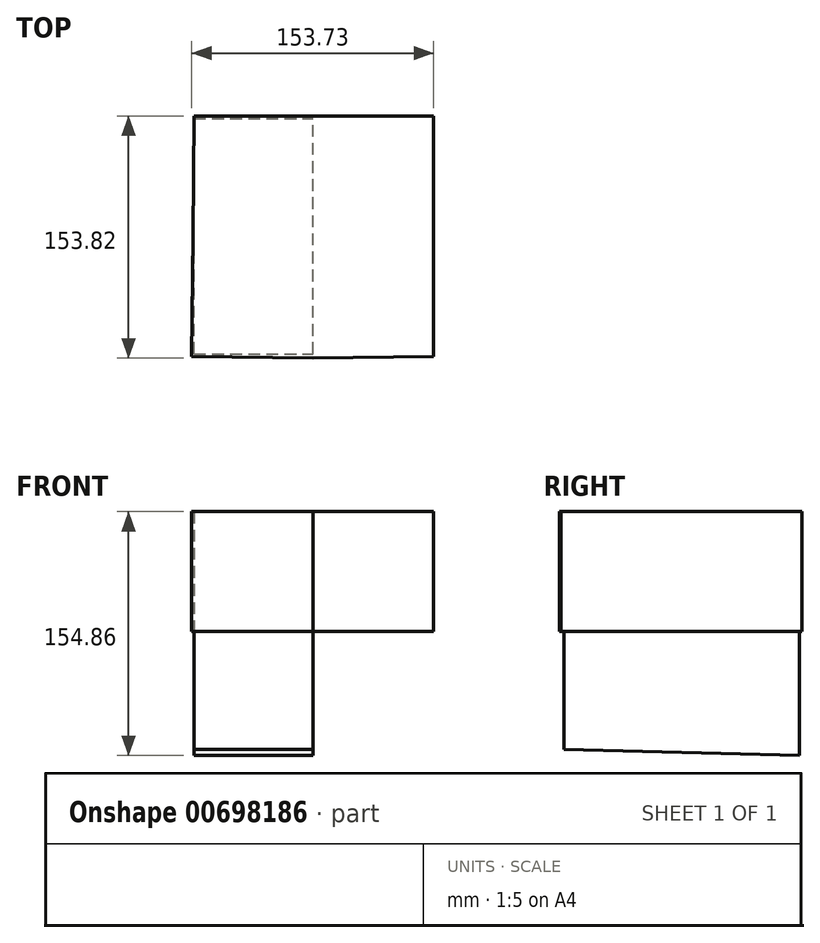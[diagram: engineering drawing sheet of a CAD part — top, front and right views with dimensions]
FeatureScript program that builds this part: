
annotation { "Feature Type Name" : "Feature", "Feature Type Description" : "" }
export const myFeature = defineFeature(function(context is Context, id is Id, definition is map)
    precondition{}
    {
        {
            var Q0;
            Q0=qCreatedBy(makeId("Top.planeOp"),FACE);
            var sketch = newSketch(context, id + "F0", { "sketchPlane" : qUnion([Q0])});
            skLineSegment(sketch, "E0", {"start": v(0, 0) * mm, "end": v(-75.67, 76.05) * mm});
            skLineSegment(sketch, "E1", {"start": v(0, 0) * mm, "end": v(76.43, 76.05) * mm});
            skLineSegment(sketch, "E2", {"start": v(0, 0) * mm, "end": v(76.43, -76.8) * mm});
            skLineSegment(sketch, "E3", {"start": v(0, 0) * mm, "end": v(-77.19, -76.8) * mm});
            skLineSegment(sketch, "E4", {"start": v(0, 0) * mm, "end": v(76.54, 0) * mm});
            skLineSegment(sketch, "E5", {"start": v(0, 0) * mm, "end": v(-76.28, 0) * mm});
            skLineSegment(sketch, "E6", {"start": v(0, 0) * mm, "end": v(0, -77.75) * mm});
            skLineSegment(sketch, "E7", {"start": v(0, 0) * mm, "end": v(0, 76.07) * mm});
            skLineSegment(sketch, "E8", {"start": v(76.43, 76.05) * mm, "end": v(0, 76.07) * mm});
            skLineSegment(sketch, "E9", {"start": v(0, 76.07) * mm, "end": v(-75.67, 76.05) * mm});
            skLineSegment(sketch, "E10", {"start": v(-75.67, 76.05) * mm, "end": v(-76.28, 0) * mm});
            skLineSegment(sketch, "E11", {"start": v(-76.28, 0) * mm, "end": v(-77.19, -76.8) * mm});
            skLineSegment(sketch, "E12", {"start": v(-77.19, -76.8) * mm, "end": v(0, -77.75) * mm});
            skLineSegment(sketch, "E13", {"start": v(0, -77.75) * mm, "end": v(76.43, -76.8) * mm});
            skLineSegment(sketch, "E14", {"start": v(76.43, -76.8) * mm, "end": v(76.54, 0) * mm});
            skLineSegment(sketch, "E15", {"start": v(76.54, 0) * mm, "end": v(76.43, 76.05) * mm});
            skSolve(sketch);
        }
        {
            var Q0;
            Q0=makeQuery(id+"F0.imprint","IMPRINT",FACE,{"disambiguationData":[TD([[makeQuery(id+"F0.imprint","IMPRINT",EDGE,{"derivedFrom":sQuery(id+"F0.wireOp",EDGE,"E0")}),1.0]])]});
            var Q1;
            Q1=makeQuery(id+"F0.imprint","IMPRINT",FACE,{"disambiguationData":[TD([[makeQuery(id+"F0.imprint","IMPRINT",EDGE,{"derivedFrom":sQuery(id+"F0.wireOp",EDGE,"E0")}),-1.0]])]});
            var Q2;
            Q2=makeQuery(id+"F0.imprint","IMPRINT",FACE,{"disambiguationData":[TD([[makeQuery(id+"F0.imprint","IMPRINT",EDGE,{"derivedFrom":sQuery(id+"F0.wireOp",EDGE,"E2")}),1.0]])]});
            var Q3;
            Q3=makeQuery(id+"F0.imprint","IMPRINT",FACE,{"disambiguationData":[TD([[makeQuery(id+"F0.imprint","IMPRINT",EDGE,{"derivedFrom":sQuery(id+"F0.wireOp",EDGE,"E2")}),-1.0]])]});
            var Q4;
            Q4=makeQuery(id+"F0.imprint","IMPRINT",FACE,{"disambiguationData":[TD([[makeQuery(id+"F0.imprint","IMPRINT",EDGE,{"derivedFrom":sQuery(id+"F0.wireOp",EDGE,"E3")}),-1.0]])]});
            var Q5;
            Q5=makeQuery(id+"F0.imprint","IMPRINT",FACE,{"disambiguationData":[TD([[makeQuery(id+"F0.imprint","IMPRINT",EDGE,{"derivedFrom":sQuery(id+"F0.wireOp",EDGE,"E3")}),1.0]])]});
            var Q6;
            Q6=makeQuery(id+"F0.imprint","IMPRINT",FACE,{"disambiguationData":[TD([[makeQuery(id+"F0.imprint","IMPRINT",EDGE,{"derivedFrom":sQuery(id+"F0.wireOp",EDGE,"E1")}),-1.0]])]});
            var Q7;
            Q7=makeQuery(id+"F0.imprint","IMPRINT",FACE,{"disambiguationData":[TD([[makeQuery(id+"F0.imprint","IMPRINT",EDGE,{"derivedFrom":sQuery(id+"F0.wireOp",EDGE,"E1")}),1.0]])]});
            extrude(context, id + "F1", {"entities" : qUnion([Q0, Q1, Q2, Q3, Q4, Q5, Q6, Q7]), "depth" : 76.2 * mm, "offsetDistance" : 25.4 * mm});
        }
        {
            var Q0;
            Q0=qCreatedBy(makeId("Right.planeOp"),FACE);
            var sketch = newSketch(context, id + "F2", { "sketchPlane" : qUnion([Q0])});
            skLineSegment(sketch, "E16", {"start": v(0, 0) * mm, "end": v(74.5, 0) * mm});
            skLineSegment(sketch, "E17", {"start": v(0, 0) * mm, "end": v(-75.03, 0) * mm});
            skLineSegment(sketch, "E18", {"start": v(0, 0) * mm, "end": v(0, 67.81) * mm});
            skLineSegment(sketch, "E19", {"start": v(0, 0) * mm, "end": v(0, -75.18) * mm});
            skLineSegment(sketch, "E20", {"start": v(74.5, 0) * mm, "end": v(74.5, -78.66) * mm});
            skLineSegment(sketch, "E21", {"start": v(-75.03, 0) * mm, "end": v(-75.03, -74.68) * mm});
            skLineSegment(sketch, "E22", {"start": v(-75.03, -74.68) * mm, "end": v(74.5, -78.66) * mm});
            skLineSegment(sketch, "E23", {"start": v(74.5, -78.66) * mm, "end": v(0, 0) * mm});
            skLineSegment(sketch, "E24", {"start": v(0, 0) * mm, "end": v(-75.03, -74.68) * mm});
            skSolve(sketch);
        }
        {
            var Q0;
            Q0=makeQuery(id+"F2.imprint","IMPRINT",FACE,{"disambiguationData":[TD([[makeQuery(id+"F2.imprint","IMPRINT",EDGE,{"derivedFrom":sQuery(id+"F2.wireOp",EDGE,"E16")}),-1.0]])]});
            var Q1;
            Q1=makeQuery(id+"F2.imprint","IMPRINT",FACE,{"disambiguationData":[TD([[makeQuery(id+"F2.imprint","IMPRINT",EDGE,{"derivedFrom":sQuery(id+"F2.wireOp",EDGE,"E22")}),1.0]])]});
            var Q2;
            Q2=makeQuery(id+"F2.imprint","IMPRINT",FACE,{"disambiguationData":[TD([[makeQuery(id+"F2.imprint","IMPRINT",EDGE,{"derivedFrom":sQuery(id+"F2.wireOp",EDGE,"E17")}),1.0]])]});
            extrude(context, id + "F3", {"entities" : qUnion([Q0, Q1, Q2]), "operationType" : NewBodyOperationType.ADD, "oppositeDirection" : true, "depth" : 75.7 * mm, "offsetDistance" : 25.4 * mm});
        }
    });
